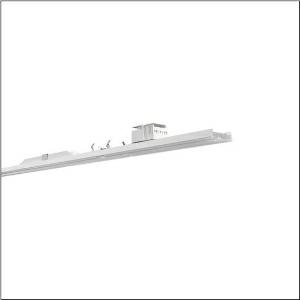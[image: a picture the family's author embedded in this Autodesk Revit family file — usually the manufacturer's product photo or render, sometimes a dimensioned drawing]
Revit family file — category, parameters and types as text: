
# Revit family: licross_r__11_recessed_ho_51tl1ecn4b5r_6c22
name_source: partatom
category: Lighting Fixtures
units: mm (PartAtom-declared; Revit-internal decimal feet)

## family parameters
Cut with Voids When Loaded = No
Host = Face
Light Source = No
Part Type = Normal
Room Calculation Point = No
Round Connector Dimension = Use Diameter
Shared = No

## types (1)
- --- (1 x LED, 11810 lm, 68.8 W, 4000K)
    Apparent Load = 69 VA
    CIE Flux Codes = 85 95 99 100 100
    Color Rendering = 80
    Color Temperature = 4000K
    Default Elevation = 1800 mm
    Description = Licross® 11 Recessed HO, luminaire insert, of sheet steel, galvanised, coil coated, white, length: 1.500mm, width: 66mm, height: 67mm, LED rated luminous flux: 11.810lm, light colour: 840, control gear: ON/OFF Multilumen, CLOi, control gear: ECG Multilumen, with plug, 3-pole, with phase selection, mains connection: 220..240V, AC, 50/60Hz, halogen-free wiring, primary optical cover: cover, of PMMA, light emission: direct distribution, protection rating (complete): IP40, insulation class (complete): insulation class I (protective earthing), certification: CE, ENEC, VDE, UKCA, protection symbol: D if used in an environment without relevant dust loads with corresponding accessories, permissible ambient temperature for indoor applications: -35..+35°C, reducing of maximum allowable ambient temperature of 5°C with ceiling mounting, corresponds to IFS (International Featured Standards) requirements for safety and quality in the food industry, LABS conformity tested according to VDMA 24364:2018-05, packaging unit: 1 piece
    Height = 58 mm
    Lamp = 1 x LED
    Lamp Light Flux = 11810 lm
    Lamp Power = 68.8 W
    Lamp count = 1
    Length = 1500 mm
    Luminous efficacy = 172 lm/W
    Manufacturer = Siteco
    ModVariant = No
    Model = 51TL1ECN4B5R
    Mounting Place = Ceiling
    Mounting Type = Pendant
    Number of Poles = 1
    OnlyDefault = Yes
    Power Factor = 1
    Product Name = Licross® 11 Recessed HO
    Product group = luminaire insert
    ProductGroupID = 902
    Protection Class = Protection class I
    Protection Degree = IP 40
    RLX_Detail_Level = 1
    RlxData = <blob elided: 20357 chars, md5=48584c42>
    Socket = socket
    Standby Power = 0 W
    System Light Flux = 11810 lm
    System Power = 69 W
    Type Comments = factory setting: luminous flux: 100 % | (A | C | E) | 160 mA
    Type Image = l_1266722.jpg
    URL = http://relux.com
    VarID = @adj_092445
    Voltage = 0 V
    Weight = 0.00 kg
    Width = 66 mm

## geometry (parser evidence)
native form markers: Blend x4, Sweep x11
no freeform markers — native parametric forms only
